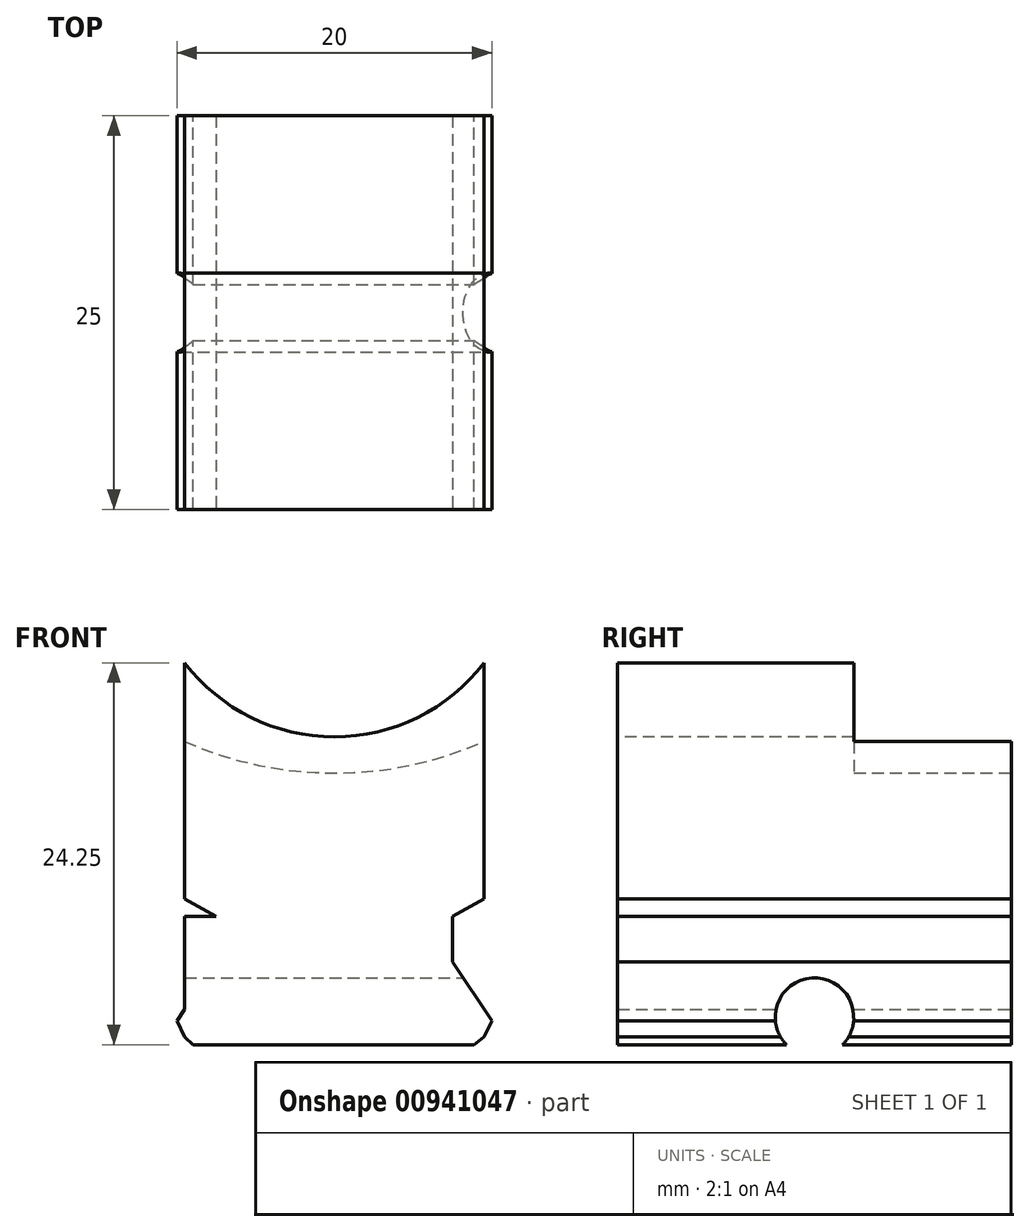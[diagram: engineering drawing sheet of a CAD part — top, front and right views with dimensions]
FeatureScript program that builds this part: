
annotation { "Feature Type Name" : "Feature", "Feature Type Description" : "" }
export const myFeature = defineFeature(function(context is Context, id is Id, definition is map)
    precondition{}
    {
        {
            var Q0;
            Q0=qCreatedBy(makeId("Front.planeOp"),FACE);
            var sketch = newSketch(context, id + "F0", { "sketchPlane" : qUnion([Q0])});
            skLineSegment(sketch, "E0.bottom", {"start": v(-1.45, 0) * mm, "end": v(17.55, 0) * mm});
            skLineSegment(sketch, "E0.top", {"start": v(-1.45, -17) * mm, "end": v(17.55, -17) * mm});
            skLineSegment(sketch, "E0.left", {"start": v(-1.45, 0) * mm, "end": v(-1.45, -17) * mm});
            skLineSegment(sketch, "E0.right", {"start": v(17.55, 0) * mm, "end": v(17.55, -17) * mm});
            skLineSegment(sketch, "E1", {"start": v(8.05, 0) * mm, "end": v(8.05, -2) * mm});
            skArc(sketch, "E2", {"start": v(-1.45, 0) * mm, "mid": v(8.05, -2) * mm, "end": v(17.55, 0) * mm});
            skLineSegment(sketch, "E3", {"start": v(-1.45, -17) * mm, "end": v(-1.95, -17) * mm});
            skLineSegment(sketch, "E4", {"start": v(17.55, -17) * mm, "end": v(18.05, -17) * mm});
            skLineSegment(sketch, "E5", {"start": v(-1.95, -17) * mm, "end": v(-1.95, -25.6) * mm});
            skLineSegment(sketch, "E6", {"start": v(18.05, -17) * mm, "end": v(18.05, -24.5) * mm});
            skLineSegment(sketch, "E7", {"start": v(-1.45, -17) * mm, "end": v(-1.95, -17.75) * mm});
            skLineSegment(sketch, "E8", {"start": v(-1.95, -17.75) * mm, "end": v(18.05, -17.75) * mm});
            skLineSegment(sketch, "E9", {"start": v(18.05, -17.75) * mm, "end": v(17.55, -17) * mm});
            skLineSegment(sketch, "E10", {"start": v(-1.95, -18.75) * mm, "end": v(18.05, -18.75) * mm});
            skLineSegment(sketch, "E11", {"start": v(-1.95, -17.75) * mm, "end": v(-1.45, -18.75) * mm});
            skLineSegment(sketch, "E12", {"start": v(18.05, -17.75) * mm, "end": v(17.55, -18.75) * mm});
            skLineSegment(sketch, "E13", {"start": v(-1.95, -19.25) * mm, "end": v(18.05, -19.25) * mm});
            skPoint(sketch, "E13.endSnap0", {"position": v(18.05, -20.75) * mm});
            skLineSegment(sketch, "E14", {"start": v(-1.45, -18.75) * mm, "end": v(-0.92, -19.25) * mm});
            skLineSegment(sketch, "E15", {"start": v(17.55, -18.75) * mm, "end": v(16.93, -19.25) * mm});
            skSolve(sketch);
        }
        {
            var Q0;
            Q0=makeQuery(id+"F0.imprint","IMPRINT",FACE,{"disambiguationData":[TD([[makeQuery(id+"F0.imprint","IMPRINT",EDGE,{"derivedFrom":sQuery(id+"F0.wireOp",EDGE,"E0.top")}),1.0]])]});
            var Q1;
            Q1=makeQuery(id+"F0.imprint","IMPRINT",FACE,{"disambiguationData":[TD([[makeQuery(id+"F0.imprint","IMPRINT",EDGE,{"derivedFrom":sQuery(id+"F0.wireOp",EDGE,"E0.top")}),-1.0]])]});
            var Q2;
            Q2=makeQuery(id+"F0.imprint","IMPRINT",FACE,{"disambiguationData":[TD([[makeQuery(id+"F0.imprint","IMPRINT",EDGE,{"derivedFrom":sQuery(id+"F0.wireOp",EDGE,"E8")}),-1.0]])]});
            var Q3;
            {var subQ0=sQuery(id+"F0.wireOp",EDGE,"E14");Q3=makeQuery(id+"F0.imprint","IMPRINT",FACE,{"disambiguationData":[TD([[makeQuery(id+"F0.imprint","IMPRINT",EDGE,{"derivedFrom":subQ0}),1.0]])]});}
            var Q4;
            {var subQ3=sQuery(id+"F0.wireOp",EDGE,"E1");Q4=makeQuery(id+"F0.imprint","IMPRINT",FACE,{"disambiguationData":[TD([[makeQuery(id+"F0.imprint","IMPRINT",EDGE,{"derivedFrom":subQ3}),-1.0]])]});}
            var Q5;
            {var subQ3=sQuery(id+"F0.wireOp",EDGE,"E1");Q5=makeQuery(id+"F0.imprint","IMPRINT",FACE,{"disambiguationData":[TD([[makeQuery(id+"F0.imprint","IMPRINT",EDGE,{"derivedFrom":subQ3}),1.0]])]});}
            extrude(context, id + "F1", {"entities" : qUnion([Q0, Q1, Q2, Q3, Q4, Q5]), "depth" : 25 * mm, "offsetDistance" : 25 * mm});
        }
        {
            var Q0;
            Q0=makeQuery(id+"F1.opExtrude","CAP_FACE",FACE,{"disambiguationData":[OSD([sQuery(id+"F0.wireOp",EDGE,"E0.top"),sQuery(id+"F0.wireOp",EDGE,"E0.left"),sQuery(id+"F0.wireOp",EDGE,"E0.right"),sQuery(id+"F0.wireOp",EDGE,"E2")])],"isStart":false});
            var sketch = newSketch(context, id + "F2", { "sketchPlane" : qUnion([Q0])});
            skLineSegment(sketch, "E16", {"start": v(-1.45, -17) * mm, "end": v(-1.45, -10) * mm});
            skLineSegment(sketch, "E17", {"start": v(-1.45, -17) * mm, "end": v(-1.45, -14) * mm});
            skLineSegment(sketch, "E18", {"start": v(-1.45, -11.1) * mm, "end": v(0.55, -11.1) * mm});
            skLineSegment(sketch, "E19", {"start": v(-1.45, -10) * mm, "end": v(0.55, -11.1) * mm});
            skLineSegment(sketch, "E20", {"start": v(0.55, -11.1) * mm, "end": v(0.55, -14) * mm});
            skLineSegment(sketch, "E21", {"start": v(0.55, -14) * mm, "end": v(-1.45, -17) * mm});
            skLineSegment(sketch, "E22", {"start": v(-1.45, -10) * mm, "end": v(17.55, -10) * mm});
            skPoint(sketch, "E22.endSnap0", {"position": v(17.55, -8.5) * mm});
            skLineSegment(sketch, "E23", {"start": v(0.55, -11.1) * mm, "end": v(15.55, -11.1) * mm});
            skLineSegment(sketch, "E24", {"start": v(17.55, -10) * mm, "end": v(15.55, -11.1) * mm});
            skLineSegment(sketch, "E25", {"start": v(15.55, -11.1) * mm, "end": v(15.55, -14) * mm});
            skLineSegment(sketch, "E26", {"start": v(15.55, -14) * mm, "end": v(17.55, -17) * mm});
            skSolve(sketch);
        }
        {
            var Q0;
            {var subQ1=sQuery(id+"F2.wireOp",EDGE,"E17");Q0=makeQuery(id+"F2.imprint","IMPRINT",FACE,{"disambiguationData":[TD([[makeQuery(id+"F2.imprint","IMPRINT",EDGE,{"derivedFrom":subQ1}),1.0]])]});}
            var Q1;
            {var subQ2=sQuery(id+"F2.wireOp",EDGE,"E18");Q1=makeQuery(id+"F2.imprint","IMPRINT",FACE,{"disambiguationData":[TD([[makeQuery(id+"F2.imprint","IMPRINT",EDGE,{"derivedFrom":subQ2}),1.0]])]});}
            var Q2;
            {var subQ0=sQuery(id+"F2.wireOp",EDGE,"E24");Q2=makeQuery(id+"F2.imprint","IMPRINT",FACE,{"disambiguationData":[TD([[makeQuery(id+"F2.imprint","IMPRINT",EDGE,{"derivedFrom":subQ0}),1.0]])]});}
            extrude(context, id + "F3", {"entities" : qUnion([Q0, Q1, Q2]), "operationType" : NewBodyOperationType.REMOVE, "oppositeDirection" : true, "depth" : 25 * mm, "offsetDistance" : 25 * mm});
        }
        {
            var Q0;
            Q0=makeQuery(id+"F1.opExtrude","CAP_FACE",FACE,{"disambiguationData":[OSD([sQuery(id+"F0.wireOp",EDGE,"E0.bottom"),sQuery(id+"F0.wireOp",EDGE,"E0.left"),sQuery(id+"F0.wireOp",EDGE,"E0.right"),sQuery(id+"F0.wireOp",EDGE,"E7"),sQuery(id+"F0.wireOp",EDGE,"E9"),sQuery(id+"F0.wireOp",EDGE,"E11"),sQuery(id+"F0.wireOp",EDGE,"E12"),sQuery(id+"F0.wireOp",EDGE,"E13"),sQuery(id+"F0.wireOp",EDGE,"E14"),sQuery(id+"F0.wireOp",EDGE,"E15")])],"isStart":true});
            var sketch = newSketch(context, id + "F4", { "sketchPlane" : qUnion([Q0])});
            skLineSegment(sketch, "E27", {"start": v(-8.05, 0) * mm, "end": v(-8.05, -2) * mm});
            skArc(sketch, "E28", {"start": v(-17.55, 0) * mm, "mid": v(-8.05, -2) * mm, "end": v(1.45, 0) * mm});
            skSolve(sketch);
        }
        {
            var Q0;
            {var subQ0=sQuery(id+"F4.wireOp",EDGE,"E27");Q0=makeQuery(id+"F4.imprint","IMPRINT",FACE,{"disambiguationData":[TD([[makeQuery(id+"F4.imprint","IMPRINT",EDGE,{"derivedFrom":subQ0}),-1.0]])]});}
            var Q1;
            {var subQ0=sQuery(id+"F4.wireOp",EDGE,"E27");Q1=makeQuery(id+"F4.imprint","IMPRINT",FACE,{"disambiguationData":[TD([[makeQuery(id+"F4.imprint","IMPRINT",EDGE,{"derivedFrom":subQ0}),1.0]])]});}
            extrude(context, id + "F5", {"entities" : qUnion([Q0, Q1]), "operationType" : NewBodyOperationType.REMOVE, "oppositeDirection" : true, "depth" : 10 * mm, "offsetDistance" : 25 * mm});
        }
        {
            var Q0;
            Q0=makeQuery(id+"F1.opExtrude","SWEPT_FACE",FACE,{"disambiguationData":[OSD([sQuery(id+"F0.wireOp",EDGE,"E0.bottom")])]});
            extrude(context, id + "F6", {"entities" : qUnion([Q0]), "operationType" : NewBodyOperationType.ADD, "depth" : 5 * mm, "offsetDistance" : 25 * mm});
        }
        {
            var Q0;
            {var subQ0=sQuery(id+"F0.wireOp",EDGE,"E0.bottom");Q0=makeQuery(id+"F6.boolean.opBoolean","MERGE",FACE,{"derivedFrom":[makeQuery(id+"F1.opExtrude","CAP_FACE",FACE,{"disambiguationData":[OSD([subQ0,sQuery(id+"F0.wireOp",EDGE,"E0.left"),sQuery(id+"F0.wireOp",EDGE,"E0.right"),sQuery(id+"F0.wireOp",EDGE,"E7"),sQuery(id+"F0.wireOp",EDGE,"E9"),sQuery(id+"F0.wireOp",EDGE,"E11"),sQuery(id+"F0.wireOp",EDGE,"E12"),sQuery(id+"F0.wireOp",EDGE,"E13"),sQuery(id+"F0.wireOp",EDGE,"E14"),sQuery(id+"F0.wireOp",EDGE,"E15")])],"isStart":false}),makeQuery(id+"F6.opExtrude","SWEPT_FACE",FACE,{"disambiguationData":[OSD([subQ0]),TDD([makeQuery(id+"F1.opExtrude","CAP_EDGE",EDGE,{"disambiguationData":[OSD([subQ0])],"isStart":false})])]})]});}
            var sketch = newSketch(context, id + "F7", { "sketchPlane" : qUnion([Q0])});
            skLineSegment(sketch, "E29", {"start": v(-1.45, 0) * mm, "end": v(17.55, 0) * mm});
            skLineSegment(sketch, "E30", {"start": v(8.05, 0) * mm, "end": v(8.05, 0.3) * mm});
            skArc(sketch, "E31", {"start": v(-1.45, 5) * mm, "mid": v(8.05, 0.3) * mm, "end": v(17.55, 5) * mm});
            skSolve(sketch);
        }
        {
            var Q0;
            Q0=qSketchRegion(id+"F7",true);
            var Q1;
            {var subQ3=sQuery(id+"F0.wireOp",EDGE,"E0.bottom");var subQ4=makeQuery(id+"F6.opExtrude","CAP_EDGE",EDGE,{"disambiguationData":[OSD([subQ3]),TDD([makeQuery(id+"F1.opExtrude","CAP_EDGE",EDGE,{"disambiguationData":[OSD([subQ3])],"isStart":false})])],"isStart":false});Q1=makeQuery(id+"F7.imprint","IMPRINT",FACE,{"disambiguationData":[TD([[makeQuery(id+"F7.imprint","IMPRINT",EDGE,{"derivedFrom":subQ4}),-1.0]])]});}
            extrude(context, id + "F8", {"entities" : qUnion([Q0, Q1]), "operationType" : NewBodyOperationType.REMOVE, "oppositeDirection" : true, "depth" : 25 * mm, "offsetDistance" : 25 * mm});
        }
        {
            var Q0;
            {var subQ0=sQuery(id+"F0.wireOp",EDGE,"E0.right");Q0=makeQuery(id+"F6.boolean.opBoolean","MERGE",FACE,{"derivedFrom":[makeQuery(id+"F1.opExtrude","SWEPT_FACE",FACE,{"disambiguationData":[OSD([subQ0])]}),makeQuery(id+"F6.opExtrude","SWEPT_FACE",FACE,{"disambiguationData":[OSD([sQuery(id+"F0.wireOp",EDGE,"E0.bottom"),subQ0,sQuery(id+"F0.wireOp",EDGE,"E2")])]})]});}
            var sketch = newSketch(context, id + "F9", { "sketchPlane" : qUnion([Q0])});
            skLineSegment(sketch, "E32", {"start": v(0, -17.5) * mm, "end": v(-10, -17.5) * mm});
            skLineSegment(sketch, "E33", {"start": v(-10, -17.5) * mm, "end": v(-15, -17.5) * mm});
            skCircle(sketch, "E34", {"center": v(-12.5, -17.5) * mm, "radius": 2.5 * mm});
            skSolve(sketch);
        }
        {
            var Q0;
            {var subQ0=sQuery(id+"F9.wireOp",EDGE,"E33");Q0=makeQuery(id+"F9.imprint","IMPRINT",FACE,{"disambiguationData":[TD([[makeQuery(id+"F9.imprint","IMPRINT",EDGE,{"derivedFrom":subQ0}),-1.0]])]});}
            var Q1;
            {var subQ0=sQuery(id+"F9.wireOp",EDGE,"E33");Q1=makeQuery(id+"F9.imprint","IMPRINT",FACE,{"disambiguationData":[TD([[makeQuery(id+"F9.imprint","IMPRINT",EDGE,{"derivedFrom":subQ0}),1.0]])]});}
            extrude(context, id + "F10", {"entities" : qUnion([Q0, Q1]), "operationType" : NewBodyOperationType.REMOVE, "oppositeDirection" : true, "depth" : 25 * mm, "offsetDistance" : 25 * mm, "hasSecondDirection" : true, "secondDirectionOppositeDirection" : false, "secondDirectionDepth" : 25 * mm});
        }
    });
